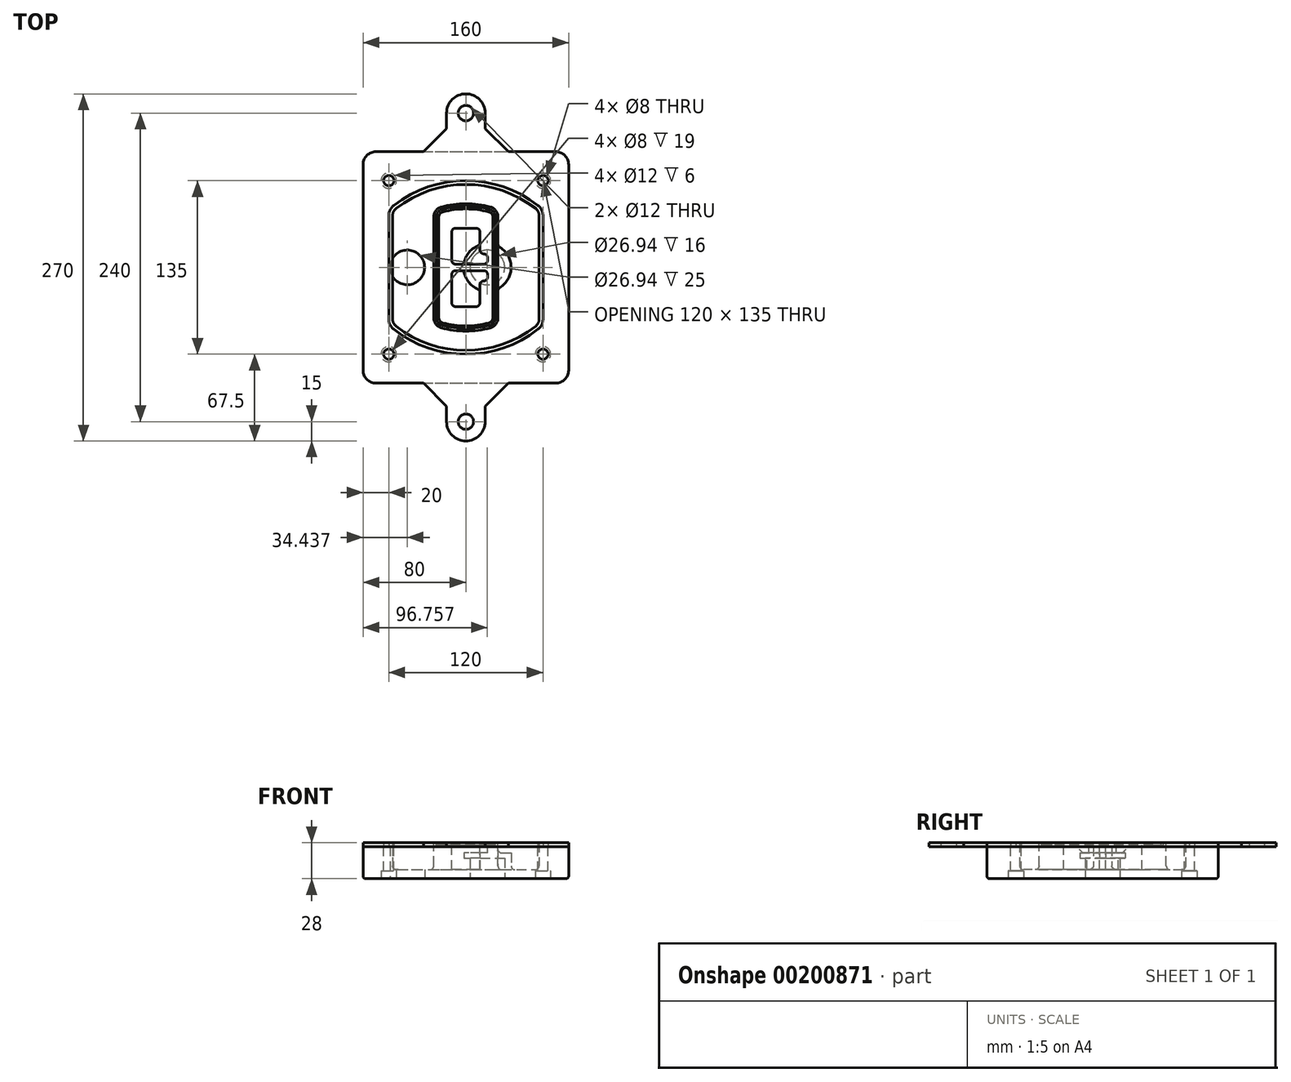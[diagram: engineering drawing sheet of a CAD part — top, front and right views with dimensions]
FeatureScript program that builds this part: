
annotation { "Feature Type Name" : "Feature", "Feature Type Description" : "" }
export const myFeature = defineFeature(function(context is Context, id is Id, definition is map)
    precondition{}
    {
        {
            var Q0;
            Q0=qCreatedBy(makeId("Top.planeOp"),FACE);
            var sketch = newSketch(context, id + "F0", { "sketchPlane" : qUnion([Q0])});
            skPoint(sketch, "E0.rect.middle", {"position": v(0, 0) * mm});
            skLineSegment(sketch, "E1.bottom", {"start": v(-70, -90) * mm, "end": v(70, -90) * mm});
            skLineSegment(sketch, "E1.top", {"start": v(-70, 90) * mm, "end": v(70, 90) * mm});
            skLineSegment(sketch, "E1.left", {"start": v(-80, -80) * mm, "end": v(-80, 80) * mm});
            skLineSegment(sketch, "E1.right", {"start": v(80, -80) * mm, "end": v(80, 80) * mm});
            skLineSegment(sketch, "E2", {"start": v(-80, 90) * mm, "end": v(80, -90) * mm, "construction": true});
            skLineSegment(sketch, "E3", {"start": v(80, 90) * mm, "end": v(-80, -90) * mm, "construction": true});
            skCircle(sketch, "E4", {"center": v(-60, 67.5) * mm, "radius": 4 * mm});
            skCircle(sketch, "E5", {"center": v(60, 67.5) * mm, "radius": 4 * mm});
            skCircle(sketch, "E6", {"center": v(60, -67.5) * mm, "radius": 4 * mm});
            skCircle(sketch, "E7", {"center": v(-60, -67.5) * mm, "radius": 4 * mm});
            skLineSegment(sketch, "E8", {"start": v(-60, 67.5) * mm, "end": v(60, 67.5) * mm, "construction": true});
            skLineSegment(sketch, "E9", {"start": v(60, 67.5) * mm, "end": v(60, -67.5) * mm, "construction": true});
            skLineSegment(sketch, "E10", {"start": v(60, -67.5) * mm, "end": v(-60, -67.5) * mm, "construction": true});
            skLineSegment(sketch, "E11", {"start": v(-60, -67.5) * mm, "end": v(-60, 67.5) * mm, "construction": true});
            skLineSegment(sketch, "E12", {"start": v(-60, 40.3) * mm, "end": v(-60, -40.3) * mm});
            skLineSegment(sketch, "E13", {"start": v(60, 40.3) * mm, "end": v(60, -40.3) * mm});
            skArc(sketch, "E14", {"start": v(56.15, 48.18) * mm, "mid": v(0, 67.5) * mm, "end": v(-56.15, 48.18) * mm});
            skArc(sketch, "E15", {"start": v(-56.15, -48.18) * mm, "mid": v(0, -67.5) * mm, "end": v(56.15, -48.18) * mm});
            skLineSegment(sketch, "E16", {"start": v(-60, 0) * mm, "end": v(60, 0) * mm, "construction": true});
            skPoint(sketch, "E17.visualSharp", {"position": v(-60, -45) * mm});
            skArc(sketch, "E17.filletArc", {"start": v(-60, -40.3) * mm, "mid": v(-58.99, -44.68) * mm, "end": v(-56.15, -48.18) * mm});
            skPoint(sketch, "E18.visualSharp", {"position": v(-60, 45) * mm});
            skArc(sketch, "E18.filletArc", {"start": v(-56.15, 48.18) * mm, "mid": v(-58.99, 44.68) * mm, "end": v(-60, 40.3) * mm});
            skPoint(sketch, "E19.visualSharp", {"position": v(60, 45) * mm});
            skArc(sketch, "E19.filletArc", {"start": v(60, 40.3) * mm, "mid": v(58.99, 44.68) * mm, "end": v(56.15, 48.18) * mm});
            skPoint(sketch, "E20.visualSharp", {"position": v(60, -45) * mm});
            skArc(sketch, "E20.filletArc", {"start": v(56.15, -48.18) * mm, "mid": v(58.99, -44.68) * mm, "end": v(60, -40.3) * mm});
            skPoint(sketch, "E21.visualSharp", {"position": v(-80, 90) * mm});
            skArc(sketch, "E21.filletArc", {"start": v(-70, 90) * mm, "mid": v(-77.07, 87.07) * mm, "end": v(-80, 80) * mm});
            skPoint(sketch, "E22.visualSharp", {"position": v(80, 90) * mm});
            skArc(sketch, "E22.filletArc", {"start": v(80, 80) * mm, "mid": v(77.07, 87.07) * mm, "end": v(70, 90) * mm});
            skPoint(sketch, "E23.visualSharp", {"position": v(80, -90) * mm});
            skArc(sketch, "E23.filletArc", {"start": v(70, -90) * mm, "mid": v(77.07, -87.07) * mm, "end": v(80, -80) * mm});
            skPoint(sketch, "E24.visualSharp", {"position": v(-80, -90) * mm});
            skArc(sketch, "E24.filletArc", {"start": v(-80, -80) * mm, "mid": v(-77.07, -87.07) * mm, "end": v(-70, -90) * mm});
            skArc(sketch, "E25.0", {"start": v(57, 40.3) * mm, "mid": v(56.3, 43.36) * mm, "end": v(54.3, 45.81) * mm});
            skLineSegment(sketch, "E25.1", {"start": v(57, 40.3) * mm, "end": v(57, -40.3) * mm});
            skArc(sketch, "E25.2", {"start": v(54.3, -45.81) * mm, "mid": v(56.3, -43.36) * mm, "end": v(57, -40.3) * mm});
            skArc(sketch, "E25.3", {"start": v(-54.3, -45.81) * mm, "mid": v(0, -64.5) * mm, "end": v(54.3, -45.81) * mm});
            skArc(sketch, "E25.4", {"start": v(-57, -40.3) * mm, "mid": v(-56.3, -43.36) * mm, "end": v(-54.3, -45.81) * mm});
            skArc(sketch, "E25.5", {"start": v(54.3, 45.81) * mm, "mid": v(0, 64.5) * mm, "end": v(-54.3, 45.81) * mm});
            skLineSegment(sketch, "E25.6", {"start": v(-57, 40.3) * mm, "end": v(-57, -40.3) * mm});
            skArc(sketch, "E25.7", {"start": v(-54.3, 45.81) * mm, "mid": v(-56.3, 43.36) * mm, "end": v(-57, 40.3) * mm});
            skArc(sketch, "E26.0", {"start": v(-58.62, 51.33) * mm, "mid": v(-62.58, 46.43) * mm, "end": v(-64, 40.3) * mm});
            skArc(sketch, "E26.1", {"start": v(58.62, 51.33) * mm, "mid": v(0, 71.5) * mm, "end": v(-58.62, 51.33) * mm});
            skArc(sketch, "E26.2", {"start": v(64, 40.3) * mm, "mid": v(62.58, 46.43) * mm, "end": v(58.62, 51.33) * mm});
            skLineSegment(sketch, "E26.3", {"start": v(64, 40.3) * mm, "end": v(64, -40.3) * mm});
            skArc(sketch, "E26.4", {"start": v(58.62, -51.33) * mm, "mid": v(62.58, -46.43) * mm, "end": v(64, -40.3) * mm});
            skLineSegment(sketch, "E26.5", {"start": v(-64, 40.3) * mm, "end": v(-64, -40.3) * mm});
            skArc(sketch, "E26.6", {"start": v(-58.62, -51.33) * mm, "mid": v(0, -71.5) * mm, "end": v(58.62, -51.33) * mm});
            skArc(sketch, "E26.7", {"start": v(-64, -40.3) * mm, "mid": v(-62.58, -46.43) * mm, "end": v(-58.62, -51.33) * mm});
            skSolve(sketch);
        }
        {
            var Q0;
            Q0=makeQuery(id+"F0.imprint","IMPRINT",FACE,{"disambiguationData":[TD([[makeQuery(id+"F0.imprint","IMPRINT",EDGE,{"derivedFrom":sQuery(id+"F0.wireOp",EDGE,"E1.bottom")}),1.0]])]});
            var Q1;
            Q1=makeQuery(id+"F0.imprint","IMPRINT",FACE,{"disambiguationData":[TD([[makeQuery(id+"F0.imprint","IMPRINT",EDGE,{"derivedFrom":sQuery(id+"F0.wireOp",EDGE,"E12")}),1.0]])]});
            var Q2;
            Q2=makeQuery(id+"F0.imprint","IMPRINT",FACE,{"disambiguationData":[TD([[makeQuery(id+"F0.imprint","IMPRINT",EDGE,{"derivedFrom":sQuery(id+"F0.wireOp",EDGE,"E25.0")}),1.0]])]});
            var Q3;
            Q3=makeQuery(id+"F0.imprint","IMPRINT",FACE,{"disambiguationData":[TD([[makeQuery(id+"F0.imprint","IMPRINT",EDGE,{"derivedFrom":sQuery(id+"F0.wireOp",EDGE,"E12")}),-1.0]])]});
            extrude(context, id + "F1", {"entities" : qUnion([Q0, Q1, Q2, Q3]), "oppositeDirection" : true, "depth" : 25 * mm});
        }
        {
            var Q0;
            Q0=makeQuery(id+"F0.imprint","IMPRINT",FACE,{"disambiguationData":[TD([[makeQuery(id+"F0.imprint","IMPRINT",EDGE,{"derivedFrom":sQuery(id+"F0.wireOp",EDGE,"E12")}),1.0]])]});
            extrude(context, id + "F2", {"entities" : qUnion([Q0]), "operationType" : NewBodyOperationType.ADD, "depth" : 3 * mm});
        }
        {
            var Q0;
            Q0=makeQuery(id+"F0.imprint","IMPRINT",FACE,{"disambiguationData":[TD([[makeQuery(id+"F0.imprint","IMPRINT",EDGE,{"derivedFrom":sQuery(id+"F0.wireOp",EDGE,"E25.0")}),1.0]])]});
            extrude(context, id + "F3", {"entities" : qUnion([Q0]), "operationType" : NewBodyOperationType.REMOVE, "oppositeDirection" : true, "depth" : 18 * mm});
        }
        {
            var Q0;
            Q0=makeQuery(id+"F2.opExtrude","CAP_FACE",FACE,{"disambiguationData":[OSD([sQuery(id+"F0.wireOp",EDGE,"E12"),sQuery(id+"F0.wireOp",EDGE,"E13"),sQuery(id+"F0.wireOp",EDGE,"E14"),sQuery(id+"F0.wireOp",EDGE,"E15"),sQuery(id+"F0.wireOp",EDGE,"E17.filletArc"),sQuery(id+"F0.wireOp",EDGE,"E18.filletArc"),sQuery(id+"F0.wireOp",EDGE,"E19.filletArc"),sQuery(id+"F0.wireOp",EDGE,"E20.filletArc"),sQuery(id+"F0.wireOp",EDGE,"E25.0"),sQuery(id+"F0.wireOp",EDGE,"E25.1"),sQuery(id+"F0.wireOp",EDGE,"E25.2"),sQuery(id+"F0.wireOp",EDGE,"E25.3"),sQuery(id+"F0.wireOp",EDGE,"E25.4"),sQuery(id+"F0.wireOp",EDGE,"E25.5"),sQuery(id+"F0.wireOp",EDGE,"E25.6"),sQuery(id+"F0.wireOp",EDGE,"E25.7")])],"isStart":false});
            var sketch = newSketch(context, id + "F4", { "sketchPlane" : qUnion([Q0])});
            skArc(sketch, "E27.0", {"start": v(-19.08, -46.97) * mm, "mid": v(0, -49.5) * mm, "end": v(19.08, -46.97) * mm});
            skArc(sketch, "E28.0", {"start": v(19.08, 46.97) * mm, "mid": v(0, 49.5) * mm, "end": v(-19.08, 46.97) * mm});
            skLineSegment(sketch, "E29", {"start": v(-25, 39.25) * mm, "end": v(-25, -39.25) * mm});
            skLineSegment(sketch, "E30", {"start": v(25, 39.25) * mm, "end": v(25, -39.25) * mm});
            skLineSegment(sketch, "E31", {"start": v(-25, 45.1) * mm, "end": v(25, 45.1) * mm, "construction": true});
            skLineSegment(sketch, "E32", {"start": v(-25, -45.1) * mm, "end": v(25, -45.1) * mm, "construction": true});
            skPoint(sketch, "E33.visualSharp", {"position": v(-25, 45.1) * mm});
            skArc(sketch, "E33.filletArc", {"start": v(-19.08, 46.97) * mm, "mid": v(-23.35, 44.11) * mm, "end": v(-25, 39.25) * mm});
            skPoint(sketch, "E34.visualSharp", {"position": v(25, 45.1) * mm});
            skArc(sketch, "E34.filletArc", {"start": v(25, 39.25) * mm, "mid": v(23.35, 44.11) * mm, "end": v(19.08, 46.97) * mm});
            skPoint(sketch, "E35.visualSharp", {"position": v(25, -45.1) * mm});
            skArc(sketch, "E35.filletArc", {"start": v(19.08, -46.97) * mm, "mid": v(23.35, -44.11) * mm, "end": v(25, -39.25) * mm});
            skPoint(sketch, "E36.visualSharp", {"position": v(-25, -45.1) * mm});
            skArc(sketch, "E36.filletArc", {"start": v(-25, -39.25) * mm, "mid": v(-23.35, -44.11) * mm, "end": v(-19.08, -46.97) * mm});
            skArc(sketch, "E37.0", {"start": v(54.3, 45.81) * mm, "mid": v(0, 64.5) * mm, "end": v(-54.3, 45.81) * mm});
            skArc(sketch, "E37.1", {"start": v(-54.3, 45.81) * mm, "mid": v(-56.3, 43.36) * mm, "end": v(-57, 40.3) * mm});
            skLineSegment(sketch, "E37.2", {"start": v(-57, 40.3) * mm, "end": v(-57, -40.3) * mm});
            skArc(sketch, "E37.3", {"start": v(-57, -40.3) * mm, "mid": v(-56.3, -43.36) * mm, "end": v(-54.3, -45.81) * mm});
            skArc(sketch, "E37.4", {"start": v(-54.3, -45.81) * mm, "mid": v(0, -64.5) * mm, "end": v(54.3, -45.81) * mm});
            skArc(sketch, "E37.5", {"start": v(54.3, -45.81) * mm, "mid": v(56.3, -43.36) * mm, "end": v(57, -40.3) * mm});
            skLineSegment(sketch, "E37.6", {"start": v(57, 40.3) * mm, "end": v(57, -40.3) * mm});
            skArc(sketch, "E37.7", {"start": v(57, 40.3) * mm, "mid": v(56.3, 43.36) * mm, "end": v(54.3, 45.81) * mm});
            skLineSegment(sketch, "E38.0", {"start": v(23, 39.25) * mm, "end": v(23, -39.25) * mm});
            skArc(sketch, "E38.1", {"start": v(18.56, -45.04) * mm, "mid": v(21.76, -42.9) * mm, "end": v(23, -39.25) * mm});
            skArc(sketch, "E38.2", {"start": v(-18.56, -45.04) * mm, "mid": v(0, -47.5) * mm, "end": v(18.56, -45.04) * mm});
            skArc(sketch, "E38.3", {"start": v(-23, -39.25) * mm, "mid": v(-21.76, -42.9) * mm, "end": v(-18.56, -45.04) * mm});
            skLineSegment(sketch, "E38.4", {"start": v(-23, 39.25) * mm, "end": v(-23, -39.25) * mm});
            skArc(sketch, "E38.5", {"start": v(23, 39.25) * mm, "mid": v(21.76, 42.9) * mm, "end": v(18.56, 45.04) * mm});
            skArc(sketch, "E38.6", {"start": v(-18.56, 45.04) * mm, "mid": v(-21.76, 42.9) * mm, "end": v(-23, 39.25) * mm});
            skArc(sketch, "E38.7", {"start": v(18.56, 45.04) * mm, "mid": v(0, 47.5) * mm, "end": v(-18.56, 45.04) * mm});
            skArc(sketch, "E39.0", {"start": v(21, 39.25) * mm, "mid": v(20.18, 41.68) * mm, "end": v(18.04, 43.1) * mm});
            skLineSegment(sketch, "E39.1", {"start": v(21, 39.25) * mm, "end": v(21, -39.25) * mm});
            skArc(sketch, "E39.2", {"start": v(18.04, -43.1) * mm, "mid": v(20.18, -41.68) * mm, "end": v(21, -39.25) * mm});
            skArc(sketch, "E39.3", {"start": v(-18.04, -43.1) * mm, "mid": v(0, -45.5) * mm, "end": v(18.04, -43.1) * mm});
            skArc(sketch, "E39.4", {"start": v(-21, -39.25) * mm, "mid": v(-20.18, -41.68) * mm, "end": v(-18.04, -43.1) * mm});
            skArc(sketch, "E39.5", {"start": v(18.04, 43.1) * mm, "mid": v(0, 45.5) * mm, "end": v(-18.04, 43.1) * mm});
            skLineSegment(sketch, "E39.6", {"start": v(-21, 39.25) * mm, "end": v(-21, -39.25) * mm});
            skArc(sketch, "E39.7", {"start": v(-18.04, 43.1) * mm, "mid": v(-20.18, 41.68) * mm, "end": v(-21, 39.25) * mm});
            skLineSegment(sketch, "E40", {"start": v(-25, 0) * mm, "end": v(25, 0) * mm, "construction": true});
            skLineSegment(sketch, "E41", {"start": v(-11, 5.5) * mm, "end": v(-11, 27.5) * mm});
            skLineSegment(sketch, "E42", {"start": v(-8, 30.5) * mm, "end": v(8, 30.5) * mm});
            skLineSegment(sketch, "E43", {"start": v(11, 27.5) * mm, "end": v(11, 13.5) * mm});
            skLineSegment(sketch, "E44", {"start": v(14, 10.5) * mm, "end": v(14, 10.5) * mm});
            skLineSegment(sketch, "E45", {"start": v(17, 7.5) * mm, "end": v(17, 5.5) * mm});
            skLineSegment(sketch, "E46", {"start": v(14, 2.5) * mm, "end": v(-8, 2.5) * mm});
            skPoint(sketch, "E47.visualSharp", {"position": v(-11, 30.5) * mm});
            skArc(sketch, "E47.filletArc", {"start": v(-8, 30.5) * mm, "mid": v(-10.12, 29.62) * mm, "end": v(-11, 27.5) * mm});
            skPoint(sketch, "E48.visualSharp", {"position": v(11, 30.5) * mm});
            skArc(sketch, "E48.filletArc", {"start": v(11, 27.5) * mm, "mid": v(10.12, 29.62) * mm, "end": v(8, 30.5) * mm});
            skPoint(sketch, "E49.visualSharp", {"position": v(11, 10.5) * mm});
            skArc(sketch, "E49.filletArc", {"start": v(11, 13.5) * mm, "mid": v(11.88, 11.38) * mm, "end": v(14, 10.5) * mm});
            skPoint(sketch, "E50.visualSharp", {"position": v(17, 10.5) * mm});
            skArc(sketch, "E50.filletArc", {"start": v(17, 7.5) * mm, "mid": v(16.12, 9.62) * mm, "end": v(14, 10.5) * mm});
            skPoint(sketch, "E51.visualSharp", {"position": v(17, 2.5) * mm});
            skArc(sketch, "E51.filletArc", {"start": v(14, 2.5) * mm, "mid": v(16.12, 3.38) * mm, "end": v(17, 5.5) * mm});
            skPoint(sketch, "E52.visualSharp", {"position": v(-11, 2.5) * mm});
            skArc(sketch, "E52.filletArc", {"start": v(-11, 5.5) * mm, "mid": v(-10.12, 3.38) * mm, "end": v(-8, 2.5) * mm});
            skLineSegment(sketch, "E53.0.MirrorCS", {"start": v(14, -2.5) * mm, "end": v(-8, -2.5) * mm});
            skArc(sketch, "E54.0.MirrorCS", {"start": v(-11, -5.5) * mm, "mid": v(-10.12, -3.38) * mm, "end": v(-8, -2.5) * mm});
            skLineSegment(sketch, "E55.0.MirrorCS", {"start": v(-11, -5.5) * mm, "end": v(-11, -27.5) * mm});
            skArc(sketch, "E56.0.MirrorCS", {"start": v(-8, -30.5) * mm, "mid": v(-10.12, -29.62) * mm, "end": v(-11, -27.5) * mm});
            skLineSegment(sketch, "E57.0.MirrorCS", {"start": v(-8, -30.5) * mm, "end": v(8, -30.5) * mm});
            skArc(sketch, "E58.0.MirrorCS", {"start": v(11, -27.5) * mm, "mid": v(10.12, -29.62) * mm, "end": v(8, -30.5) * mm});
            skLineSegment(sketch, "E59.0.MirrorCS", {"start": v(11, -27.5) * mm, "end": v(11, -13.5) * mm});
            skArc(sketch, "E60.0.MirrorCS", {"start": v(11, -13.5) * mm, "mid": v(11.88, -11.38) * mm, "end": v(14, -10.5) * mm});
            skArc(sketch, "E61.0.MirrorCS", {"start": v(17, -7.5) * mm, "mid": v(16.12, -9.62) * mm, "end": v(14, -10.5) * mm});
            skLineSegment(sketch, "E62.0.MirrorCS", {"start": v(17, -7.5) * mm, "end": v(17, -5.5) * mm});
            skArc(sketch, "E63.0.MirrorCS", {"start": v(14, -2.5) * mm, "mid": v(16.12, -3.38) * mm, "end": v(17, -5.5) * mm});
            skSolve(sketch);
        }
        {
            var Q0;
            Q0=makeQuery(id+"F4.imprint","IMPRINT",FACE,{"disambiguationData":[TD([[makeQuery(id+"F4.imprint","IMPRINT",EDGE,{"derivedFrom":sQuery(id+"F4.wireOp",EDGE,"E27.0")}),1.0]])]});
            var Q1;
            Q1=makeQuery(id+"F4.imprint","IMPRINT",FACE,{"disambiguationData":[TD([[makeQuery(id+"F4.imprint","IMPRINT",EDGE,{"derivedFrom":sQuery(id+"F4.wireOp",EDGE,"E38.0")}),-1.0]])]});
            var Q2;
            Q2=makeQuery(id+"F4.imprint","IMPRINT",FACE,{"disambiguationData":[TD([[makeQuery(id+"F4.imprint","IMPRINT",EDGE,{"derivedFrom":sQuery(id+"F4.wireOp",EDGE,"E39.0")}),1.0]])]});
            extrude(context, id + "F5", {"entities" : qUnion([Q0, Q1, Q2]), "operationType" : NewBodyOperationType.ADD, "endBound" : BoundingType.UP_TO_NEXT, "oppositeDirection" : true, "depth" : 25 * mm});
        }
        {
            var Q0;
            Q0=makeQuery(id+"F4.imprint","IMPRINT",FACE,{"disambiguationData":[TD([[makeQuery(id+"F4.imprint","IMPRINT",EDGE,{"derivedFrom":sQuery(id+"F4.wireOp",EDGE,"E38.0")}),-1.0]])]});
            extrude(context, id + "F6", {"entities" : qUnion([Q0]), "operationType" : NewBodyOperationType.REMOVE, "oppositeDirection" : true, "depth" : 2 * mm});
        }
        {
            var Q0;
            Q0=makeQuery(id+"F1.opExtrude","CAP_FACE",FACE,{"disambiguationData":[OSD([sQuery(id+"F0.wireOp",EDGE,"E1.bottom"),sQuery(id+"F0.wireOp",EDGE,"E1.top"),sQuery(id+"F0.wireOp",EDGE,"E1.left"),sQuery(id+"F0.wireOp",EDGE,"E1.right"),sQuery(id+"F0.wireOp",EDGE,"E4"),sQuery(id+"F0.wireOp",EDGE,"E5"),sQuery(id+"F0.wireOp",EDGE,"E6"),sQuery(id+"F0.wireOp",EDGE,"E7"),sQuery(id+"F0.wireOp",EDGE,"E21.filletArc"),sQuery(id+"F0.wireOp",EDGE,"E22.filletArc"),sQuery(id+"F0.wireOp",EDGE,"E23.filletArc"),sQuery(id+"F0.wireOp",EDGE,"E24.filletArc")])],"isStart":false});
            var sketch = newSketch(context, id + "F7", { "sketchPlane" : qUnion([Q0])});
            skCircle(sketch, "E64", {"center": v(16.76, 0) * mm, "radius": 13.47 * mm});
            skCircle(sketch, "E65", {"center": v(-45.56, 0) * mm, "radius": 13.47 * mm});
            skLineSegment(sketch, "E66", {"start": v(80, 0) * mm, "end": v(-80, 0) * mm});
            skCircle(sketch, "E67", {"center": v(16.76, 0) * mm, "radius": 18.47 * mm});
            skCircle(sketch, "E68", {"center": v(60, -67.5) * mm, "radius": 6 * mm});
            skCircle(sketch, "E69", {"center": v(-60, -67.5) * mm, "radius": 6 * mm});
            skCircle(sketch, "E70", {"center": v(-60, 67.5) * mm, "radius": 6 * mm});
            skCircle(sketch, "E71", {"center": v(60, 67.5) * mm, "radius": 6 * mm});
            skSolve(sketch);
        }
        {
            var Q0;
            {var subQ1=sQuery(id+"F7.wireOp",EDGE,"E66");var subQ4=sQuery(id+"F7.wireOp",EDGE,"E64");var subQ6=makeQuery(id+"F7.imprint","INTERSECT",VERTEX,{"disambiguationData":[OD(0.0)],"derivedFrom":[subQ4,subQ1]});Q0=makeQuery(id+"F7.imprint","IMPRINT",FACE,{"disambiguationData":[TD([[makeQuery(id+"F7.imprint","IMPRINT",EDGE,{"disambiguationData":[TD([[subQ6,-1.0]])],"derivedFrom":subQ4}),-1.0]])]});}
            var Q1;
            {var subQ0=sQuery(id+"F7.wireOp",EDGE,"E66");var subQ1=sQuery(id+"F7.wireOp",EDGE,"E64");var subQ3=makeQuery(id+"F7.imprint","INTERSECT",VERTEX,{"disambiguationData":[OD(0.0)],"derivedFrom":[subQ1,subQ0]});Q1=makeQuery(id+"F7.imprint","IMPRINT",FACE,{"disambiguationData":[TD([[makeQuery(id+"F7.imprint","IMPRINT",EDGE,{"disambiguationData":[TD([[subQ3,-1.0]])],"derivedFrom":subQ1}),1.0]])]});}
            var Q2;
            {var subQ0=sQuery(id+"F7.wireOp",EDGE,"E66");var subQ1=sQuery(id+"F7.wireOp",EDGE,"E64");var subQ3=makeQuery(id+"F7.imprint","INTERSECT",VERTEX,{"disambiguationData":[OD(0.0)],"derivedFrom":[subQ1,subQ0]});Q2=makeQuery(id+"F7.imprint","IMPRINT",FACE,{"disambiguationData":[TD([[makeQuery(id+"F7.imprint","IMPRINT",EDGE,{"disambiguationData":[TD([[subQ3,1.0]])],"derivedFrom":subQ1}),1.0]])]});}
            var Q3;
            {var subQ1=sQuery(id+"F7.wireOp",EDGE,"E66");var subQ4=sQuery(id+"F7.wireOp",EDGE,"E64");var subQ6=makeQuery(id+"F7.imprint","INTERSECT",VERTEX,{"disambiguationData":[OD(0.0)],"derivedFrom":[subQ4,subQ1]});Q3=makeQuery(id+"F7.imprint","IMPRINT",FACE,{"disambiguationData":[TD([[makeQuery(id+"F7.imprint","IMPRINT",EDGE,{"disambiguationData":[TD([[subQ6,1.0]])],"derivedFrom":subQ4}),-1.0]])]});}
            extrude(context, id + "F8", {"entities" : qUnion([Q0, Q1, Q2, Q3]), "operationType" : NewBodyOperationType.ADD, "oppositeDirection" : true, "depth" : 20 * mm});
        }
        {
            var Q0;
            {var subQ0=sQuery(id+"F7.wireOp",EDGE,"E66");var subQ1=sQuery(id+"F7.wireOp",EDGE,"E64");var subQ3=makeQuery(id+"F7.imprint","INTERSECT",VERTEX,{"disambiguationData":[OD(0.0)],"derivedFrom":[subQ1,subQ0]});Q0=makeQuery(id+"F7.imprint","IMPRINT",FACE,{"disambiguationData":[TD([[makeQuery(id+"F7.imprint","IMPRINT",EDGE,{"disambiguationData":[TD([[subQ3,-1.0]])],"derivedFrom":subQ1}),1.0]])]});}
            var Q1;
            {var subQ0=sQuery(id+"F7.wireOp",EDGE,"E66");var subQ1=sQuery(id+"F7.wireOp",EDGE,"E64");var subQ3=makeQuery(id+"F7.imprint","INTERSECT",VERTEX,{"disambiguationData":[OD(0.0)],"derivedFrom":[subQ1,subQ0]});Q1=makeQuery(id+"F7.imprint","IMPRINT",FACE,{"disambiguationData":[TD([[makeQuery(id+"F7.imprint","IMPRINT",EDGE,{"disambiguationData":[TD([[subQ3,1.0]])],"derivedFrom":subQ1}),1.0]])]});}
            extrude(context, id + "F9", {"entities" : qUnion([Q0, Q1]), "operationType" : NewBodyOperationType.REMOVE, "oppositeDirection" : true, "depth" : 16 * mm});
        }
        {
            var Q0;
            {var subQ0=sQuery(id+"F7.wireOp",EDGE,"E66");var subQ1=sQuery(id+"F7.wireOp",EDGE,"E65");var subQ3=makeQuery(id+"F7.imprint","INTERSECT",VERTEX,{"disambiguationData":[OD(0.0)],"derivedFrom":[subQ1,subQ0]});Q0=makeQuery(id+"F7.imprint","IMPRINT",FACE,{"disambiguationData":[TD([[makeQuery(id+"F7.imprint","IMPRINT",EDGE,{"disambiguationData":[TD([[subQ3,-1.0]])],"derivedFrom":subQ1}),1.0]])]});}
            var Q1;
            {var subQ0=sQuery(id+"F7.wireOp",EDGE,"E66");var subQ1=sQuery(id+"F7.wireOp",EDGE,"E65");var subQ3=makeQuery(id+"F7.imprint","INTERSECT",VERTEX,{"disambiguationData":[OD(0.0)],"derivedFrom":[subQ1,subQ0]});Q1=makeQuery(id+"F7.imprint","IMPRINT",FACE,{"disambiguationData":[TD([[makeQuery(id+"F7.imprint","IMPRINT",EDGE,{"disambiguationData":[TD([[subQ3,1.0]])],"derivedFrom":subQ1}),1.0]])]});}
            extrude(context, id + "F10", {"entities" : qUnion([Q0, Q1]), "operationType" : NewBodyOperationType.REMOVE, "oppositeDirection" : true, "depth" : 25 * mm});
        }
        {
            var Q0;
            Q0=makeQuery(id+"F7.imprint","IMPRINT",FACE,{"disambiguationData":[TD([[makeQuery(id+"F7.imprint","IMPRINT",EDGE,{"derivedFrom":sQuery(id+"F7.wireOp",EDGE,"E68")}),1.0]])]});
            var Q1;
            Q1=makeQuery(id+"F7.imprint","IMPRINT",FACE,{"disambiguationData":[TD([[makeQuery(id+"F7.imprint","IMPRINT",EDGE,{"derivedFrom":makeQuery(id+"F1.opExtrude","CAP_EDGE",EDGE,{"disambiguationData":[OSD([sQuery(id+"F0.wireOp",EDGE,"E5")])],"isStart":false})}),-1.0]])]});
            var Q2;
            Q2=makeQuery(id+"F7.imprint","IMPRINT",FACE,{"disambiguationData":[TD([[makeQuery(id+"F7.imprint","IMPRINT",EDGE,{"derivedFrom":sQuery(id+"F7.wireOp",EDGE,"E69")}),1.0]])]});
            var Q3;
            Q3=makeQuery(id+"F7.imprint","IMPRINT",FACE,{"disambiguationData":[TD([[makeQuery(id+"F7.imprint","IMPRINT",EDGE,{"derivedFrom":makeQuery(id+"F1.opExtrude","CAP_EDGE",EDGE,{"disambiguationData":[OSD([sQuery(id+"F0.wireOp",EDGE,"E4")])],"isStart":false})}),-1.0]])]});
            var Q4;
            Q4=makeQuery(id+"F7.imprint","IMPRINT",FACE,{"disambiguationData":[TD([[makeQuery(id+"F7.imprint","IMPRINT",EDGE,{"derivedFrom":sQuery(id+"F7.wireOp",EDGE,"E70")}),1.0]])]});
            var Q5;
            Q5=makeQuery(id+"F7.imprint","IMPRINT",FACE,{"disambiguationData":[TD([[makeQuery(id+"F7.imprint","IMPRINT",EDGE,{"derivedFrom":makeQuery(id+"F1.opExtrude","CAP_EDGE",EDGE,{"disambiguationData":[OSD([sQuery(id+"F0.wireOp",EDGE,"E7")])],"isStart":false})}),-1.0]])]});
            var Q6;
            Q6=makeQuery(id+"F7.imprint","IMPRINT",FACE,{"disambiguationData":[TD([[makeQuery(id+"F7.imprint","IMPRINT",EDGE,{"derivedFrom":sQuery(id+"F7.wireOp",EDGE,"E71")}),1.0]])]});
            var Q7;
            Q7=makeQuery(id+"F7.imprint","IMPRINT",FACE,{"disambiguationData":[TD([[makeQuery(id+"F7.imprint","IMPRINT",EDGE,{"derivedFrom":makeQuery(id+"F1.opExtrude","CAP_EDGE",EDGE,{"disambiguationData":[OSD([sQuery(id+"F0.wireOp",EDGE,"E6")])],"isStart":false})}),-1.0]])]});
            extrude(context, id + "F11", {"entities" : qUnion([Q0, Q1, Q2, Q3, Q4, Q5, Q6, Q7]), "operationType" : NewBodyOperationType.REMOVE, "oppositeDirection" : true, "depth" : 6 * mm});
        }
        {
            var Q0;
            Q0=makeQuery(id+"F9.boolean.opBoolean","COPY",FACE,{"derivedFrom":makeQuery(id+"F9.opExtrude","CAP_FACE",FACE,{"disambiguationData":[OSD([sQuery(id+"F7.wireOp",EDGE,"E64")])],"isStart":false})});
            var sketch = newSketch(context, id + "F12", { "sketchPlane" : qUnion([Q0])});
            skArc(sketch, "E72.0", {"start": v(11, 17.55) * mm, "mid": v(2.57, 11.82) * mm, "end": v(-1.54, 2.5) * mm});
            skArc(sketch, "E72.1", {"start": v(-1.54, -2.5) * mm, "mid": v(2.57, -11.82) * mm, "end": v(11, -17.55) * mm});
            skLineSegment(sketch, "E73", {"start": v(-1.54, -2.5) * mm, "end": v(14, -2.5) * mm});
            skLineSegment(sketch, "E74.0", {"start": v(14, 2.5) * mm, "end": v(-1.54, 2.5) * mm});
            skArc(sketch, "E74.1", {"start": v(14, 2.5) * mm, "mid": v(16.12, 3.38) * mm, "end": v(17, 5.5) * mm});
            skLineSegment(sketch, "E74.2", {"start": v(17, 7.5) * mm, "end": v(17, 5.5) * mm});
            skArc(sketch, "E74.3", {"start": v(17, 7.5) * mm, "mid": v(16.12, 9.62) * mm, "end": v(14, 10.5) * mm});
            skArc(sketch, "E74.4", {"start": v(11, 13.5) * mm, "mid": v(11.88, 11.38) * mm, "end": v(14, 10.5) * mm});
            skLineSegment(sketch, "E74.5", {"start": v(11, 17.55) * mm, "end": v(11, 13.5) * mm});
            skLineSegment(sketch, "E74.7", {"start": v(14, -2.5) * mm, "end": v(-1.54, -2.5) * mm});
            skArc(sketch, "E74.8", {"start": v(14, -2.5) * mm, "mid": v(16.12, -3.38) * mm, "end": v(17, -5.5) * mm});
            skLineSegment(sketch, "E74.9", {"start": v(17, -7.5) * mm, "end": v(17, -5.5) * mm});
            skArc(sketch, "E74.10", {"start": v(17, -7.5) * mm, "mid": v(16.12, -9.62) * mm, "end": v(14, -10.5) * mm});
            skArc(sketch, "E74.11", {"start": v(11, -13.5) * mm, "mid": v(11.88, -11.38) * mm, "end": v(14, -10.5) * mm});
            skLineSegment(sketch, "E74.12", {"start": v(11, -17.55) * mm, "end": v(11, -13.5) * mm});
            skPoint(sketch, "E75.orphan", {"position": v(11, -27.5) * mm});
            skPoint(sketch, "E76.orphan", {"position": v(-8, -2.5) * mm});
            skPoint(sketch, "E77.orphan", {"position": v(-8, 2.5) * mm});
            skPoint(sketch, "E78.orphan", {"position": v(11, 27.5) * mm});
            skSolve(sketch);
        }
        {
            var Q0;
            {var subQ7=sQuery(id+"F12.wireOp",EDGE,"E72.0");var subQ14=sQuery(id+"F12.wireOp",EDGE,"E72.1");var subQ16=sQuery(id+"F12.wireOp",EDGE,"E74.1");var subQ18=sQuery(id+"F12.wireOp",EDGE,"E74.8");Q0=qUnion([makeQuery(id+"F12.imprint","IMPRINT",FACE,{"disambiguationData":[TD([[makeQuery(id+"F12.imprint","IMPRINT",EDGE,{"derivedFrom":subQ7}),1.0]])]}),makeQuery(id+"F12.imprint","IMPRINT",FACE,{"disambiguationData":[TD([[makeQuery(id+"F12.imprint","IMPRINT",EDGE,{"derivedFrom":subQ14}),1.0]])]}),makeQuery(id+"F12.imprint","IMPRINT",FACE,{"disambiguationData":[TD([[makeQuery(id+"F12.imprint","IMPRINT",EDGE,{"derivedFrom":subQ16}),1.0]])]}),makeQuery(id+"F12.imprint","IMPRINT",FACE,{"disambiguationData":[TD([[makeQuery(id+"F12.imprint","IMPRINT",EDGE,{"derivedFrom":subQ18}),-1.0]])]})]);}
            var Q1;
            Q1=makeQuery(id+"F5.boolean.opBoolean","SPLIT",FACE,{"disambiguationData":[TD([makeQuery(id+"F5.opExtrude","SWEPT_FACE",FACE,{"disambiguationData":[OSD([sQuery(id+"F4.wireOp",EDGE,"E41")])]})])],"derivedFrom":makeQuery(id+"F3.boolean.opBoolean","COPY",FACE,{"derivedFrom":makeQuery(id+"F3.opExtrude","CAP_FACE",FACE,{"disambiguationData":[OSD([sQuery(id+"F0.wireOp",EDGE,"E25.0"),sQuery(id+"F0.wireOp",EDGE,"E25.1"),sQuery(id+"F0.wireOp",EDGE,"E25.2"),sQuery(id+"F0.wireOp",EDGE,"E25.3"),sQuery(id+"F0.wireOp",EDGE,"E25.4"),sQuery(id+"F0.wireOp",EDGE,"E25.5"),sQuery(id+"F0.wireOp",EDGE,"E25.6"),sQuery(id+"F0.wireOp",EDGE,"E25.7")])],"isStart":false})})});
            extrude(context, id + "F13", {"entities" : qUnion([Q0]), "operationType" : NewBodyOperationType.REMOVE, "endBound" : BoundingType.UP_TO_SURFACE, "endBoundEntityFace" : qUnion([Q1]), "depth" : 25 * mm});
        }
        {
            var Q0;
            Q0=makeQuery(id+"F3.boolean.opBoolean","COPY",EDGE,{"derivedFrom":makeQuery(id+"F3.opExtrude","CAP_EDGE",EDGE,{"disambiguationData":[OSD([sQuery(id+"F0.wireOp",EDGE,"E25.6")])],"isStart":false})});
            var Q1;
            Q1=makeQuery(id+"F8.boolean.opBoolean","INTERSECT",EDGE,{"derivedFrom":[makeQuery(id+"F5.opExtrude","SWEPT_FACE",FACE,{"disambiguationData":[OSD([sQuery(id+"F4.wireOp",EDGE,"E30")])]}),makeQuery(id+"F8.opExtrude","CAP_FACE",FACE,{"disambiguationData":[OSD([sQuery(id+"F7.wireOp",EDGE,"E67")])],"isStart":false})]});
            var Q2;
            Q2=makeQuery(id+"F8.boolean.opBoolean","INTERSECT",EDGE,{"disambiguationData":[OD(1.0)],"derivedFrom":[makeQuery(id+"F5.opExtrude","SWEPT_FACE",FACE,{"disambiguationData":[OSD([sQuery(id+"F4.wireOp",EDGE,"E30")])]}),makeQuery(id+"F8.opExtrude","SWEPT_FACE",FACE,{"disambiguationData":[OSD([sQuery(id+"F7.wireOp",EDGE,"E67")])]})]});
            var Q3;
            {var subQ0=sQuery(id+"F4.wireOp",EDGE,"E30");Q3=makeQuery(id+"F8.boolean.opBoolean","SPLIT",EDGE,{"disambiguationData":[TD([makeQuery(id+"F5.opExtrude","SWEPT_FACE",FACE,{"disambiguationData":[OSD([sQuery(id+"F4.wireOp",EDGE,"E35.filletArc")])]})])],"derivedFrom":makeQuery(id+"F5.opExtrude","CAP_EDGE",EDGE,{"disambiguationData":[OSD([subQ0])],"isStart":false})});}
            var Q4;
            {var subQ0=sQuery(id+"F0.wireOp",EDGE,"E25.7");var subQ1=sQuery(id+"F0.wireOp",EDGE,"E25.1");var subQ2=sQuery(id+"F0.wireOp",EDGE,"E25.6");var subQ3=sQuery(id+"F0.wireOp",EDGE,"E25.5");var subQ4=sQuery(id+"F0.wireOp",EDGE,"E25.4");var subQ5=sQuery(id+"F0.wireOp",EDGE,"E25.0");var subQ6=sQuery(id+"F0.wireOp",EDGE,"E25.2");var subQ7=sQuery(id+"F0.wireOp",EDGE,"E25.3");Q4=makeQuery(id+"F8.boolean.opBoolean","INTERSECT",EDGE,{"derivedFrom":[makeQuery(id+"F5.boolean.opBoolean","SPLIT",FACE,{"disambiguationData":[TD([makeQuery(id+"F2.opExtrude","SWEPT_FACE",FACE,{"disambiguationData":[OSD([subQ5])]})])],"derivedFrom":makeQuery(id+"F3.boolean.opBoolean","COPY",FACE,{"derivedFrom":makeQuery(id+"F3.opExtrude","CAP_FACE",FACE,{"disambiguationData":[OSD([subQ5,subQ1,subQ6,subQ7,subQ4,subQ3,subQ2,subQ0])],"isStart":false})})}),makeQuery(id+"F8.opExtrude","SWEPT_FACE",FACE,{"disambiguationData":[OSD([sQuery(id+"F7.wireOp",EDGE,"E67")])]})]});}
            var Q5;
            Q5=makeQuery(id+"F8.boolean.opBoolean","INTERSECT",EDGE,{"disambiguationData":[OD(0.0)],"derivedFrom":[makeQuery(id+"F5.opExtrude","SWEPT_FACE",FACE,{"disambiguationData":[OSD([sQuery(id+"F4.wireOp",EDGE,"E30")])]}),makeQuery(id+"F8.opExtrude","SWEPT_FACE",FACE,{"disambiguationData":[OSD([sQuery(id+"F7.wireOp",EDGE,"E67")])]})]});
            fillet(context, id + "F14", {"entities" : qUnion([Q0, Q1, Q2, Q3, Q4, Q5]), "radius" : 3 * mm, "tangentPropagation" : true, "allowEdgeOverflow" : false});
        }
        {
            var Q0;
            Q0=makeQuery(id+"F1.opExtrude","CAP_EDGE",EDGE,{"disambiguationData":[OSD([sQuery(id+"F0.wireOp",EDGE,"E1.bottom")])],"isStart":false});
            fillet(context, id + "F15", {"entities" : qUnion([Q0]), "radius" : 2 * mm, "tangentPropagation" : true, "allowEdgeOverflow" : false});
        }
        {
            var Q0;
            {var subQ0=sQuery(id+"F0.wireOp",EDGE,"E22.filletArc");var subQ1=sQuery(id+"F0.wireOp",EDGE,"E7");var subQ2=sQuery(id+"F0.wireOp",EDGE,"E6");var subQ3=sQuery(id+"F0.wireOp",EDGE,"E5");var subQ4=sQuery(id+"F0.wireOp",EDGE,"E4");var subQ5=sQuery(id+"F0.wireOp",EDGE,"E1.bottom");var subQ6=sQuery(id+"F0.wireOp",EDGE,"E21.filletArc");var subQ7=sQuery(id+"F0.wireOp",EDGE,"E1.top");var subQ8=sQuery(id+"F0.wireOp",EDGE,"E1.left");var subQ9=sQuery(id+"F0.wireOp",EDGE,"E1.right");var subQ10=sQuery(id+"F0.wireOp",EDGE,"E23.filletArc");var subQ11=sQuery(id+"F0.wireOp",EDGE,"E24.filletArc");Q0=makeQuery(id+"F2.boolean.opBoolean","SPLIT",FACE,{"disambiguationData":[TD([makeQuery(id+"F1.opExtrude","SWEPT_FACE",FACE,{"disambiguationData":[OSD([subQ5])]})])],"derivedFrom":makeQuery(id+"F1.opExtrude","CAP_FACE",FACE,{"disambiguationData":[OSD([subQ5,subQ7,subQ8,subQ9,subQ4,subQ3,subQ2,subQ1,subQ6,subQ0,subQ10,subQ11])],"isStart":true})});}
            var sketch = newSketch(context, id + "F16", { "sketchPlane" : qUnion([Q0])});
            skLineSegment(sketch, "E79.0", {"start": v(80, -80) * mm, "end": v(80, 80) * mm});
            skLineSegment(sketch, "E79.1", {"start": v(60, 40.3) * mm, "end": v(60, -40.3) * mm});
            skArc(sketch, "E80.0", {"start": v(-56.15, -48.18) * mm, "mid": v(0, -67.5) * mm, "end": v(56.15, -48.18) * mm});
            skArc(sketch, "E80.1", {"start": v(56.15, -48.18) * mm, "mid": v(58.99, -44.68) * mm, "end": v(60, -40.3) * mm});
            skLineSegment(sketch, "E81.0", {"start": v(-70, -90) * mm, "end": v(70, -90) * mm});
            skArc(sketch, "E81.1", {"start": v(70, -90) * mm, "mid": v(77.07, -87.07) * mm, "end": v(80, -80) * mm});
            skLineSegment(sketch, "E81.2", {"start": v(-80, -80) * mm, "end": v(-80, 80) * mm});
            skArc(sketch, "E81.3", {"start": v(-80, -80) * mm, "mid": v(-77.07, -87.07) * mm, "end": v(-70, -90) * mm});
            skLineSegment(sketch, "E81.4", {"start": v(-70, 90) * mm, "end": v(70, 90) * mm});
            skArc(sketch, "E81.5", {"start": v(80, 80) * mm, "mid": v(77.07, 87.07) * mm, "end": v(70, 90) * mm});
            skArc(sketch, "E81.6", {"start": v(-70, 90) * mm, "mid": v(-77.07, 87.07) * mm, "end": v(-80, 80) * mm});
            skArc(sketch, "E81.7", {"start": v(56.15, 48.18) * mm, "mid": v(0, 67.5) * mm, "end": v(-56.15, 48.18) * mm});
            skLineSegment(sketch, "E81.8", {"start": v(-60, 40.3) * mm, "end": v(-60, -40.3) * mm});
            skArc(sketch, "E81.12", {"start": v(60, 40.3) * mm, "mid": v(58.99, 44.68) * mm, "end": v(56.15, 48.18) * mm});
            skArc(sketch, "E81.13", {"start": v(-56.15, 48.18) * mm, "mid": v(-58.99, 44.68) * mm, "end": v(-60, 40.3) * mm});
            skCircle(sketch, "E82.0", {"center": v(-60, -67.5) * mm, "radius": 4 * mm});
            skCircle(sketch, "E82.1", {"center": v(60, -67.5) * mm, "radius": 4 * mm});
            skCircle(sketch, "E82.2", {"center": v(60, 67.5) * mm, "radius": 4 * mm});
            skCircle(sketch, "E82.3", {"center": v(-60, 67.5) * mm, "radius": 4 * mm});
            skLineSegment(sketch, "E83", {"start": v(0, 90) * mm, "end": v(0, 120) * mm, "construction": true});
            skCircle(sketch, "E84", {"center": v(0, 120) * mm, "radius": 6 * mm});
            skLineSegment(sketch, "E85", {"start": v(-33, 90) * mm, "end": v(-15, 108) * mm});
            skLineSegment(sketch, "E86", {"start": v(-15, 108) * mm, "end": v(-15, 120) * mm});
            skLineSegment(sketch, "E87", {"start": v(33, 90) * mm, "end": v(15, 108) * mm});
            skLineSegment(sketch, "E88", {"start": v(15, 108) * mm, "end": v(15, 120) * mm});
            skArc(sketch, "E89", {"start": v(15, 120) * mm, "mid": v(0, 135) * mm, "end": v(-15, 120) * mm});
            skLineSegment(sketch, "E90", {"start": v(-80, 0) * mm, "end": v(80, 0) * mm, "construction": true});
            skLineSegment(sketch, "E91.MirrorCS", {"start": v(33, -90) * mm, "end": v(15, -108) * mm});
            skLineSegment(sketch, "E92.MirrorCS", {"start": v(-33, -90) * mm, "end": v(-15, -108) * mm});
            skLineSegment(sketch, "E93.MirrorCS", {"start": v(0, -90) * mm, "end": v(0, -120) * mm, "construction": true});
            skArc(sketch, "E94.MirrorCS", {"start": v(15, -120) * mm, "mid": v(0, -135) * mm, "end": v(-15, -120) * mm});
            skLineSegment(sketch, "E95.MirrorCS", {"start": v(15, -108) * mm, "end": v(15, -120) * mm});
            skLineSegment(sketch, "E96.MirrorCS", {"start": v(-15, -108) * mm, "end": v(-15, -120) * mm});
            skCircle(sketch, "E97.MirrorC", {"center": v(0, -120) * mm, "radius": 6 * mm});
            skArc(sketch, "E98.0", {"start": v(-60, -40.3) * mm, "mid": v(-58.99, -44.68) * mm, "end": v(-56.15, -48.18) * mm});
            skSolve(sketch);
        }
        {
            var Q0;
            Q0 = qSketchRegion(id + "F16", true);
            var Q1;
            Q1=makeQuery(id+"F2.opExtrude","CAP_FACE",FACE,{"disambiguationData":[OSD([sQuery(id+"F0.wireOp",EDGE,"E12"),sQuery(id+"F0.wireOp",EDGE,"E13"),sQuery(id+"F0.wireOp",EDGE,"E14"),sQuery(id+"F0.wireOp",EDGE,"E15"),sQuery(id+"F0.wireOp",EDGE,"E17.filletArc"),sQuery(id+"F0.wireOp",EDGE,"E18.filletArc"),sQuery(id+"F0.wireOp",EDGE,"E19.filletArc"),sQuery(id+"F0.wireOp",EDGE,"E20.filletArc"),sQuery(id+"F0.wireOp",EDGE,"E25.0"),sQuery(id+"F0.wireOp",EDGE,"E25.1"),sQuery(id+"F0.wireOp",EDGE,"E25.2"),sQuery(id+"F0.wireOp",EDGE,"E25.3"),sQuery(id+"F0.wireOp",EDGE,"E25.4"),sQuery(id+"F0.wireOp",EDGE,"E25.5"),sQuery(id+"F0.wireOp",EDGE,"E25.6"),sQuery(id+"F0.wireOp",EDGE,"E25.7")])],"isStart":false});
            extrude(context, id + "F17", {"entities" : qUnion([Q0]), "endBound" : BoundingType.UP_TO_SURFACE, "endBoundEntityFace" : qUnion([Q1]), "depth" : 25 * mm});
        }
    });
